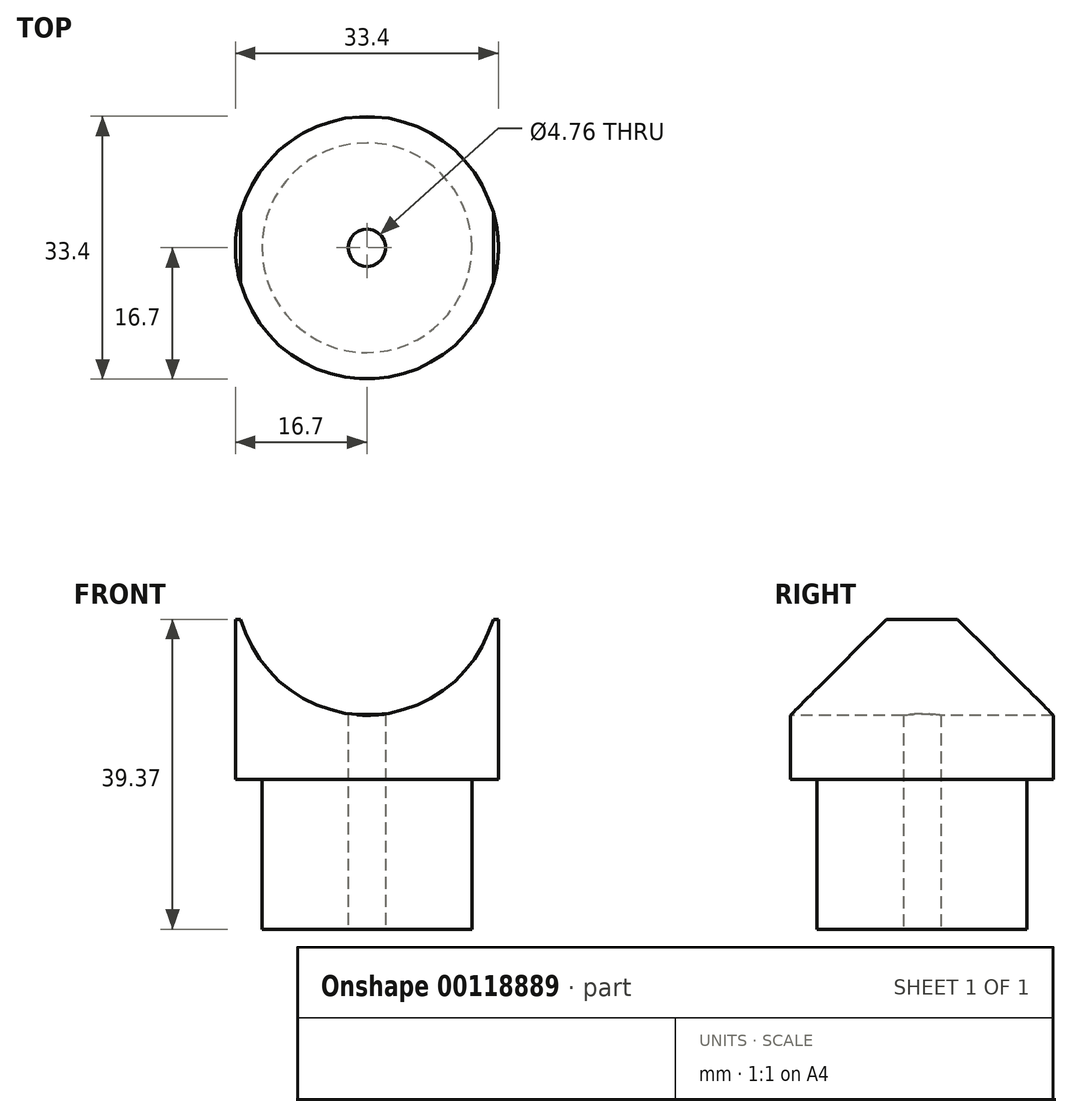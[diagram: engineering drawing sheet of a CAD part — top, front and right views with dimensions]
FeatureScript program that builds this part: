
annotation { "Feature Type Name" : "Feature", "Feature Type Description" : "" }
export const myFeature = defineFeature(function(context is Context, id is Id, definition is map)
    precondition{}
    {
        {
            var Q0;
            Q0=qCreatedBy(makeId("Front.planeOp"),FACE);
            var sketch = newSketch(context, id + "F0", { "sketchPlane" : qUnion([Q0])});
            skLineSegment(sketch, "E0", {"start": v(0, 0) * mm, "end": v(-13.32, 0) * mm});
            skLineSegment(sketch, "E1", {"start": v(-13.32, 0) * mm, "end": v(-13.32, 19.05) * mm});
            skLineSegment(sketch, "E2", {"start": v(-13.32, 19.05) * mm, "end": v(-16.7, 19.05) * mm});
            skLineSegment(sketch, "E3", {"start": v(-16.7, 19.05) * mm, "end": v(-16.7, 39.37) * mm});
            skLineSegment(sketch, "E4", {"start": v(-16.7, 39.37) * mm, "end": v(0, 39.37) * mm});
            skLineSegment(sketch, "E5", {"start": v(0, 39.37) * mm, "end": v(0, 0) * mm});
            skSolve(sketch);
        }
        {
            var Q0;
            Q0=qSketchRegion(id+"F0",true);
            var Q1;
            Q1=sQuery(id+"F0.wireOp",EDGE,"E5");
            revolve(context, id + "F1", {"entities" : qUnion([Q0]), "axis" : qUnion([Q1]), "revolveType" : RevolveType.FULL});
        }
        {
            var Q0;
            Q0=makeQuery(id+"F1.opRevolve","SWEPT_FACE",FACE,{"disambiguationData":[OSD([sQuery(id+"F0.wireOp",EDGE,"E0")])]});
            var sketch = newSketch(context, id + "F2", { "sketchPlane" : qUnion([Q0])});
            skCircle(sketch, "E6", {"center": v(0, 0) * mm, "radius": 2.38 * mm});
            skSolve(sketch);
        }
        {
            var Q0;
            Q0=qSketchRegion(id+"F2",true);
            extrude(context, id + "F3", {"entities" : qUnion([Q0]), "operationType" : NewBodyOperationType.REMOVE, "endBound" : BoundingType.THROUGH_ALL, "oppositeDirection" : true, "depth" : 25.4 * mm});
        }
        {
            var Q0;
            Q0=qCreatedBy(makeId("Front.planeOp"),FACE);
            var sketch = newSketch(context, id + "F4", { "sketchPlane" : qUnion([Q0])});
            skCircle(sketch, "E7", {"center": v(0, 43.88) * mm, "radius": 16.7 * mm});
            skSolve(sketch);
        }
        {
            var Q0;
            Q0=qSketchRegion(id+"F4",true);
            extrude(context, id + "F5", {"entities" : qUnion([Q0]), "operationType" : NewBodyOperationType.REMOVE, "endBound" : BoundingType.THROUGH_ALL, "oppositeDirection" : true, "depth" : 25.4 * mm, "hasSecondDirection" : true, "secondDirectionBound" : SecondDirectionBoundingType.THROUGH_ALL, "secondDirectionOppositeDirection" : false, "secondDirectionDepth" : 25.4 * mm});
        }
    });
